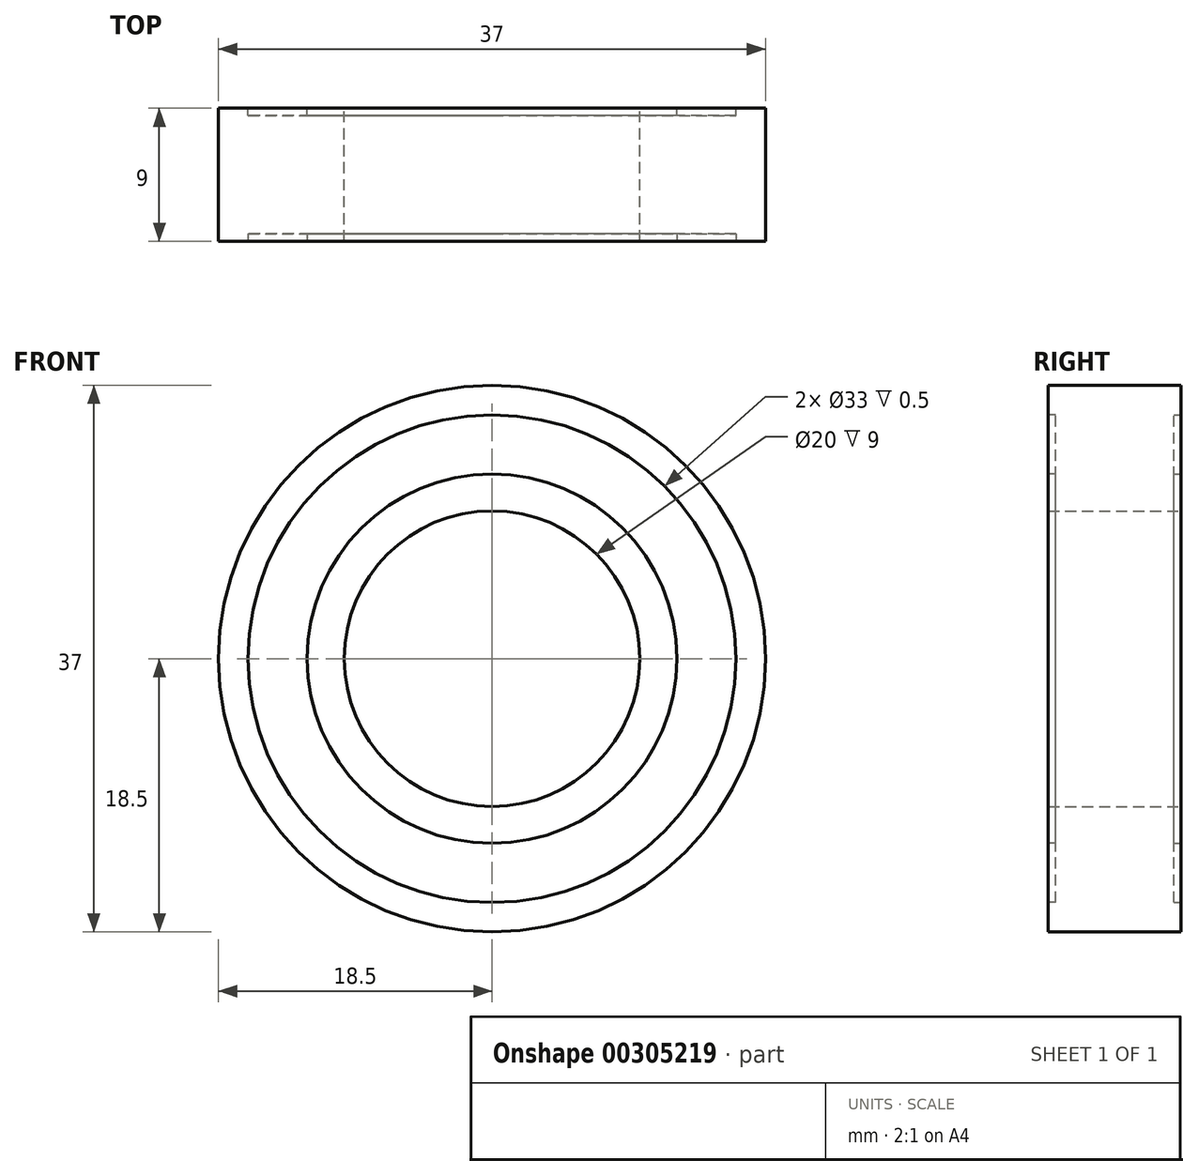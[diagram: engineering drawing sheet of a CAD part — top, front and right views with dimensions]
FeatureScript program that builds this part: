
annotation { "Feature Type Name" : "Feature", "Feature Type Description" : "" }
export const myFeature = defineFeature(function(context is Context, id is Id, definition is map)
    precondition{}
    {
        {
            var Q0;
            Q0=qCreatedBy(makeId("Front.planeOp"),FACE);
            var sketch = newSketch(context, id + "F0", { "sketchPlane" : qUnion([Q0])});
            skCircle(sketch, "E0", {"center": v(0, 0) * mm, "radius": 18.5 * mm});
            skCircle(sketch, "E1", {"center": v(0, 0) * mm, "radius": 10 * mm});
            skSolve(sketch);
        }
        {
            var Q0;
            Q0=makeQuery(id+"F0.imprint","IMPRINT",FACE,{"disambiguationData":[TD([[makeQuery(id+"F0.imprint","IMPRINT",EDGE,{"derivedFrom":sQuery(id+"F0.wireOp",EDGE,"E0")}),1.0]])]});
            extrude(context, id + "F1", {"entities" : qUnion([Q0]), "depth" : 9 * mm});
        }
        {
            var Q0;
            Q0=makeQuery(id+"F1.opExtrude","CAP_FACE",FACE,{"disambiguationData":[OSD([sQuery(id+"F0.wireOp",EDGE,"E0"),sQuery(id+"F0.wireOp",EDGE,"E1")])],"isStart":false});
            var sketch = newSketch(context, id + "F2", { "sketchPlane" : qUnion([Q0])});
            skCircle(sketch, "E2", {"center": v(0, 0) * mm, "radius": 16.5 * mm});
            skCircle(sketch, "E3", {"center": v(0, 0) * mm, "radius": 12.5 * mm});
            skSolve(sketch);
        }
        {
            var Q0;
            Q0 = qSketchRegion(id + "F2", true);
            extrude(context, id + "F3", {"entities" : qUnion([Q0]), "operationType" : NewBodyOperationType.REMOVE, "oppositeDirection" : true, "depth" : 0.5 * mm});
        }
        {
            var Q0;
            Q0=qCreatedBy(makeId("Front.planeOp"),FACE);
            var sketch = newSketch(context, id + "F4", { "sketchPlane" : qUnion([Q0])});
            skCircle(sketch, "E4", {"center": v(0, 0) * mm, "radius": 16.5 * mm});
            skCircle(sketch, "E5", {"center": v(0, 0) * mm, "radius": 12.5 * mm});
            skSolve(sketch);
        }
        {
            var Q0;
            Q0=makeQuery(id+"F4.imprint","IMPRINT",FACE,{"disambiguationData":[TD([[makeQuery(id+"F4.imprint","IMPRINT",EDGE,{"derivedFrom":sQuery(id+"F4.wireOp",EDGE,"E4")}),1.0]])]});
            extrude(context, id + "F5", {"entities" : qUnion([Q0]), "operationType" : NewBodyOperationType.REMOVE, "depth" : 0.5 * mm});
        }
    });
